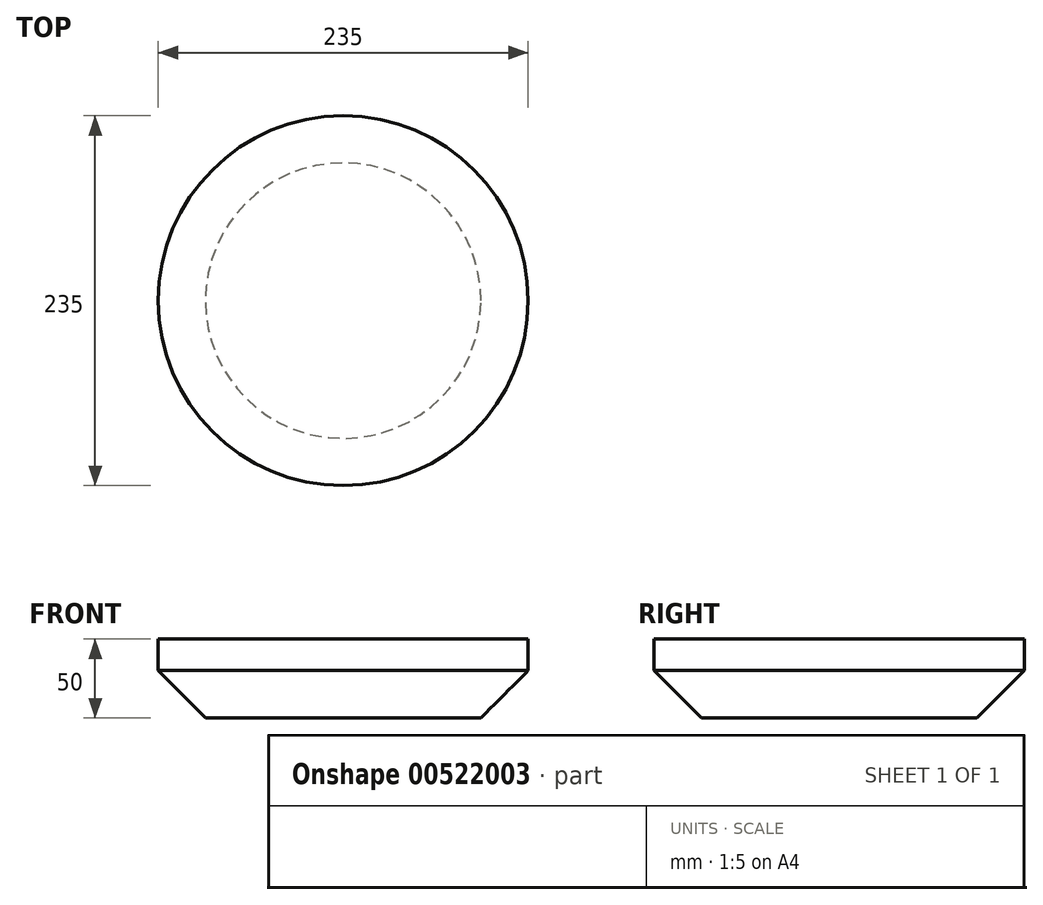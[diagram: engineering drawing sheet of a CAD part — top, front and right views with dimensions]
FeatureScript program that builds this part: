
annotation { "Feature Type Name" : "Feature", "Feature Type Description" : "" }
export const myFeature = defineFeature(function(context is Context, id is Id, definition is map)
    precondition{}
    {
        {
            var Q0;
            Q0=qCreatedBy(makeId("Top.planeOp"),FACE);
            var sketch = newSketch(context, id + "F0", { "sketchPlane" : qUnion([Q0])});
            skCircle(sketch, "E0", {"center": v(0, 0) * mm, "radius": 117.5 * mm});
            skSolve(sketch);
        }
        {
            var Q0;
            Q0=makeQuery(id+"F0.imprint","IMPRINT",FACE,{"disambiguationData":[TD([[makeQuery(id+"F0.imprint","IMPRINT",EDGE,{"derivedFrom":sQuery(id+"F0.wireOp",EDGE,"E0")}),1.0]])]});
            extrude(context, id + "F1", {"entities" : qUnion([Q0]), "depth" : 50 * mm, "offsetDistance" : 25 * mm});
        }
        {
            var Q0;
            Q0=makeQuery(id+"F1.opExtrude","CAP_EDGE",EDGE,{"disambiguationData":[OSD([sQuery(id+"F0.wireOp",EDGE,"E0")])],"isStart":true});
            chamfer(context, id + "F2", {"entities" : qUnion([Q0]), "width" : 30 * mm, "tangentPropagation" : true});
        }
    });
